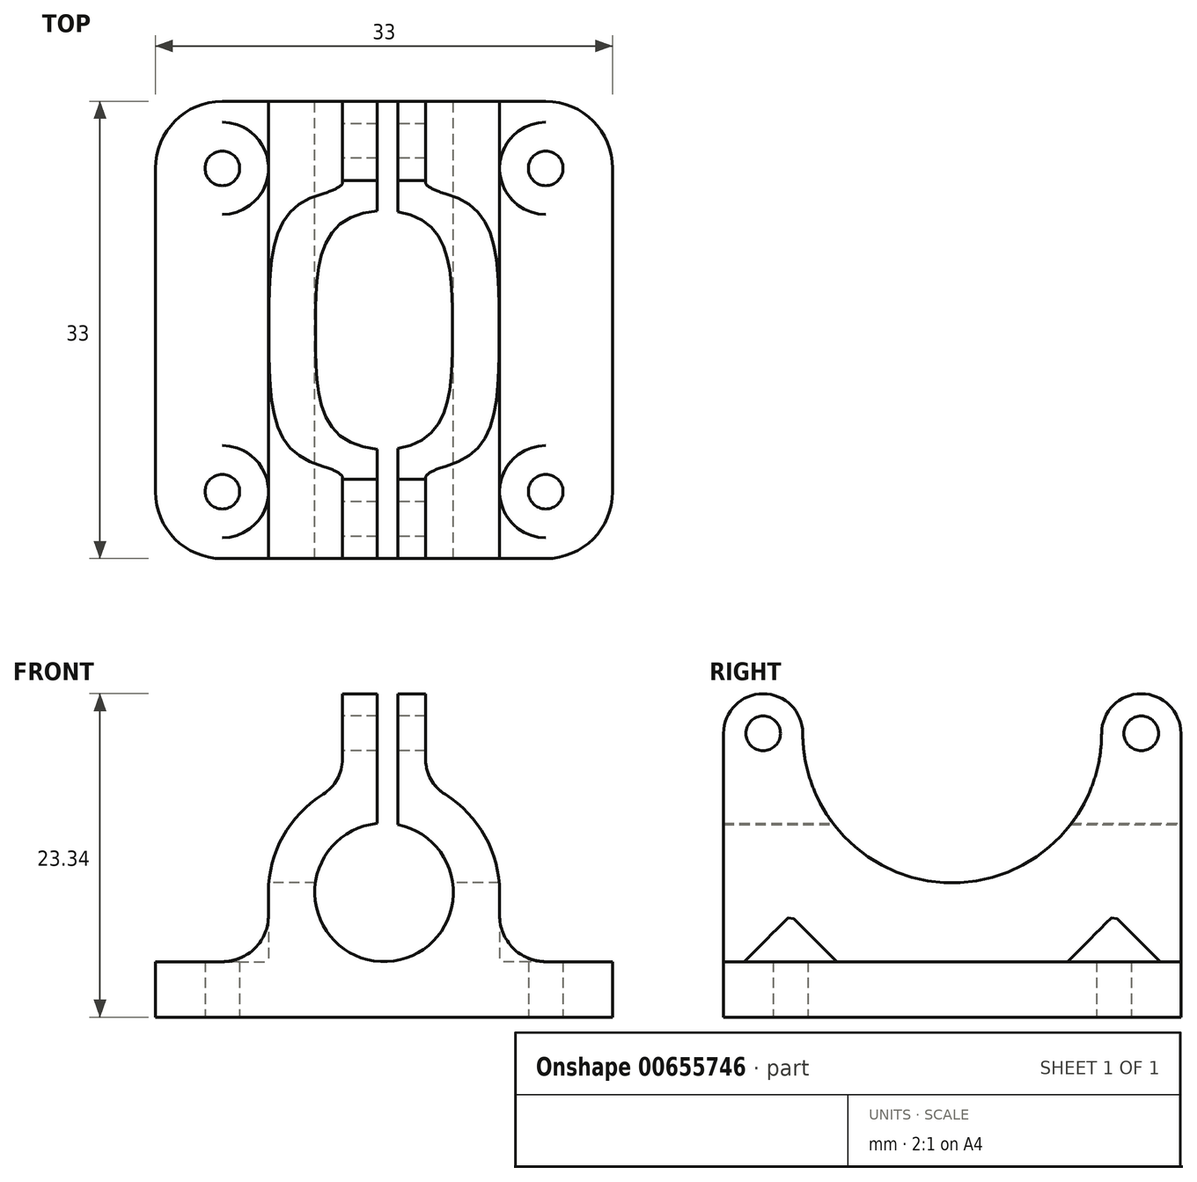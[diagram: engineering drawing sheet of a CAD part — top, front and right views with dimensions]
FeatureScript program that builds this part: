
annotation { "Feature Type Name" : "Feature", "Feature Type Description" : "" }
export const myFeature = defineFeature(function(context is Context, id is Id, definition is map)
    precondition{}
    {
        {
            var Q0;
            Q0=qCreatedBy(makeId("Top.planeOp"),FACE);
            var sketch = newSketch(context, id + "F0", { "sketchPlane" : qUnion([Q0])});
            skLineSegment(sketch, "E0", {"start": v(0, 0) * mm, "end": v(33, 33) * mm});
            skLineSegment(sketch, "E1", {"start": v(16.5, 16.5) * mm, "end": v(28.17, 28.17) * mm});
            skCircle(sketch, "E2", {"center": v(28.17, 28.17) * mm, "radius": 1.25 * mm});
            skCircle(sketch, "E3.1.0", {"center": v(4.83, 28.17) * mm, "radius": 1.25 * mm});
            skCircle(sketch, "E3.2.0", {"center": v(4.83, 4.83) * mm, "radius": 1.25 * mm});
            skCircle(sketch, "E3.3.0", {"center": v(28.17, 4.83) * mm, "radius": 1.25 * mm});
            skPoint(sketch, "E3.center", {"position": v(16.5, 16.5) * mm});
            skArc(sketch, "E4", {"start": v(28.17, 33) * mm, "mid": v(31.58, 31.58) * mm, "end": v(33, 28.17) * mm});
            skArc(sketch, "E5.1.0", {"start": v(0, 28.17) * mm, "mid": v(1.42, 31.58) * mm, "end": v(4.83, 33) * mm});
            skArc(sketch, "E5.2.0", {"start": v(4.83, 0) * mm, "mid": v(1.42, 1.42) * mm, "end": v(0, 4.83) * mm});
            skArc(sketch, "E5.3.0", {"start": v(33, 4.83) * mm, "mid": v(31.58, 1.42) * mm, "end": v(28.17, 0) * mm});
            skLineSegment(sketch, "E6", {"start": v(4.83, 33) * mm, "end": v(28.17, 33) * mm});
            skLineSegment(sketch, "E7", {"start": v(33, 28.17) * mm, "end": v(33, 4.83) * mm});
            skLineSegment(sketch, "E8", {"start": v(28.17, 0) * mm, "end": v(4.83, 0) * mm});
            skLineSegment(sketch, "E9", {"start": v(0, 4.83) * mm, "end": v(0, 28.17) * mm});
            skSolve(sketch);
        }
        {
            var Q0;
            Q0=makeQuery(id+"F0.imprint","IMPRINT",FACE,{"disambiguationData":[TD([[makeQuery(id+"F0.imprint","IMPRINT",EDGE,{"derivedFrom":sQuery(id+"F0.wireOp",EDGE,"E3.1.0")}),-1.0]])]});
            var Q1;
            Q1=makeQuery(id+"F0.imprint","IMPRINT",FACE,{"disambiguationData":[TD([[makeQuery(id+"F0.imprint","IMPRINT",EDGE,{"derivedFrom":sQuery(id+"F0.wireOp",EDGE,"E3.3.0")}),-1.0]])]});
            extrude(context, id + "F1", {"entities" : qUnion([Q0, Q1]), "depth" : 4 * mm, "offsetDistance" : 25 * mm});
        }
        {
            var Q0;
            Q0=qCreatedBy(makeId("Front.planeOp"),FACE);
            var sketch = newSketch(context, id + "F2", { "sketchPlane" : qUnion([Q0])});
            skLineSegment(sketch, "E10", {"start": v(0, 0) * mm, "end": v(0, 4) * mm});
            skCircle(sketch, "E11", {"center": v(16.5, 9) * mm, "radius": 5 * mm});
            skArc(sketch, "E12", {"start": v(4.82, 4) * mm, "mid": v(7.2, 4.98) * mm, "end": v(8.16, 7.36) * mm});
            skLineSegment(sketch, "E13", {"start": v(8.16, 7.36) * mm, "end": v(8.16, 9) * mm});
            skArc(sketch, "E14", {"start": v(24.84, 9) * mm, "mid": v(16.5, 17.34) * mm, "end": v(8.16, 9) * mm});
            skArc(sketch, "E15.MirrorCS", {"start": v(28.18, 4) * mm, "mid": v(25.8, 4.98) * mm, "end": v(24.84, 7.36) * mm});
            skLineSegment(sketch, "E16.MirrorCS", {"start": v(24.84, 7.36) * mm, "end": v(24.84, 9) * mm});
            skLineSegment(sketch, "E17", {"start": v(4.82, 4) * mm, "end": v(28.18, 4) * mm});
            skSolve(sketch);
        }
        {
            var Q0;
            Q0 = qSketchRegion(id + "F2", true);
            extrude(context, id + "F3", {"entities" : qUnion([Q0]), "operationType" : NewBodyOperationType.ADD, "oppositeDirection" : true, "depth" : 33 * mm, "offsetDistance" : 25 * mm});
        }
        {
            var Q0;
            Q0=makeQuery(id+"F3.boolean.opBoolean","MERGE",FACE,{"derivedFrom":[makeQuery(id+"F1.opExtrude","SWEPT_FACE",FACE,{"disambiguationData":[OSD([sQuery(id+"F0.wireOp",EDGE,"E6")])]}),makeQuery(id+"F3.opExtrude","CAP_FACE",FACE,{"disambiguationData":[OSD([sQuery(id+"F2.wireOp",EDGE,"E12"),sQuery(id+"F2.wireOp",EDGE,"E13"),sQuery(id+"F2.wireOp",EDGE,"E14"),sQuery(id+"F2.wireOp",EDGE,"E15.MirrorCS"),sQuery(id+"F2.wireOp",EDGE,"E16.MirrorCS"),sQuery(id+"F2.wireOp",EDGE,"E17")])],"isStart":false})]});
            var sketch = newSketch(context, id + "F4", { "sketchPlane" : qUnion([Q0])});
            skPoint(sketch, "E18.first.point", {"position": v(-24.84, 9) * mm});
            skPoint(sketch, "E18.second.point", {"position": v(-8.16, 9) * mm});
            skPoint(sketch, "E18.third.point", {"position": v(-15.36, 17.26) * mm});
            skCircle(sketch, "E19", {"center": v(-16.5, 9) * mm, "radius": 5 * mm});
            skSolve(sketch);
        }
        {
            var Q0;
            Q0 = qSketchRegion(id + "F4", true);
            extrude(context, id + "F5", {"entities" : qUnion([Q0]), "operationType" : NewBodyOperationType.REMOVE, "endBound" : BoundingType.THROUGH_ALL, "oppositeDirection" : true, "depth" : 25 * mm, "offsetDistance" : 25 * mm});
        }
        {
            var Q0;
            Q0=makeQuery(id+"F1.opExtrude","CAP_FACE",FACE,{"disambiguationData":[OSD([sQuery(id+"F0.wireOp",EDGE,"E2"),sQuery(id+"F0.wireOp",EDGE,"E3.1.0"),sQuery(id+"F0.wireOp",EDGE,"E3.2.0"),sQuery(id+"F0.wireOp",EDGE,"E3.3.0"),sQuery(id+"F0.wireOp",EDGE,"E4"),sQuery(id+"F0.wireOp",EDGE,"E5.1.0"),sQuery(id+"F0.wireOp",EDGE,"E5.2.0"),sQuery(id+"F0.wireOp",EDGE,"E5.3.0"),sQuery(id+"F0.wireOp",EDGE,"E6"),sQuery(id+"F0.wireOp",EDGE,"E7"),sQuery(id+"F0.wireOp",EDGE,"E8"),sQuery(id+"F0.wireOp",EDGE,"E9")])],"isStart":true});
            var sketch = newSketch(context, id + "F6", { "sketchPlane" : qUnion([Q0])});
            skCircle(sketch, "E20", {"center": v(28.17, -4.83) * mm, "radius": 1.25 * mm});
            skPoint(sketch, "E20.first.point", {"position": v(27.08, -4.22) * mm});
            skPoint(sketch, "E20.second.point", {"position": v(29.02, -5.75) * mm});
            skPoint(sketch, "E20.third.point", {"position": v(29.04, -3.94) * mm});
            skLineSegment(sketch, "E21", {"start": v(28.17, -4.83) * mm, "end": v(4.83, -28.17) * mm});
            skCircle(sketch, "E22.1.0", {"center": v(4.83, -4.83) * mm, "radius": 1.25 * mm});
            skCircle(sketch, "E22.2.0", {"center": v(4.83, -28.17) * mm, "radius": 1.25 * mm});
            skCircle(sketch, "E22.3.0", {"center": v(28.17, -28.17) * mm, "radius": 1.25 * mm});
            skPoint(sketch, "E22.center", {"position": v(16.5, -16.5) * mm});
            skSolve(sketch);
        }
        {
            var Q0;
            Q0=makeQuery(id+"F6.imprint","IMPRINT",FACE,{"disambiguationData":[TD([[makeQuery(id+"F6.imprint","IMPRINT",EDGE,{"derivedFrom":sQuery(id+"F6.wireOp",EDGE,"E22.1.0")}),-1.0]])]});
            var Q1;
            Q1=makeQuery(id+"F6.imprint","IMPRINT",FACE,{"disambiguationData":[TD([[makeQuery(id+"F6.imprint","IMPRINT",EDGE,{"derivedFrom":sQuery(id+"F6.wireOp",EDGE,"E20")}),-1.0]])]});
            var Q2;
            Q2=makeQuery(id+"F6.imprint","IMPRINT",FACE,{"disambiguationData":[TD([[makeQuery(id+"F6.imprint","IMPRINT",EDGE,{"derivedFrom":sQuery(id+"F6.wireOp",EDGE,"E22.3.0")}),-1.0]])]});
            var Q3;
            Q3=makeQuery(id+"F6.imprint","IMPRINT",FACE,{"disambiguationData":[TD([[makeQuery(id+"F6.imprint","IMPRINT",EDGE,{"derivedFrom":sQuery(id+"F6.wireOp",EDGE,"E22.2.0")}),-1.0]])]});
            extrude(context, id + "F7", {"entities" : qUnion([Q0, Q1, Q2, Q3]), "operationType" : NewBodyOperationType.REMOVE, "endBound" : BoundingType.THROUGH_ALL, "oppositeDirection" : true, "depth" : 25 * mm, "offsetDistance" : 25 * mm});
        }
        {
            var Q0;
            Q0=makeQuery(id+"F3.boolean.opBoolean","MERGE",FACE,{"derivedFrom":[makeQuery(id+"F1.opExtrude","SWEPT_FACE",FACE,{"disambiguationData":[OSD([sQuery(id+"F0.wireOp",EDGE,"E6")])]}),makeQuery(id+"F3.opExtrude","CAP_FACE",FACE,{"disambiguationData":[OSD([sQuery(id+"F2.wireOp",EDGE,"E12"),sQuery(id+"F2.wireOp",EDGE,"E13"),sQuery(id+"F2.wireOp",EDGE,"E14"),sQuery(id+"F2.wireOp",EDGE,"E15.MirrorCS"),sQuery(id+"F2.wireOp",EDGE,"E16.MirrorCS"),sQuery(id+"F2.wireOp",EDGE,"E17")])],"isStart":false})]});
            var sketch = newSketch(context, id + "F8", { "sketchPlane" : qUnion([Q0])});
            skLineSegment(sketch, "E23", {"start": v(-16.5, 23.34) * mm, "end": v(-14.5, 23.34) * mm});
            skLineSegment(sketch, "E24", {"start": v(-13.5, 22.34) * mm, "end": v(-13.5, 18.62) * mm});
            skPoint(sketch, "E25.visualSharp", {"position": v(-13.5, 16.78) * mm});
            skArc(sketch, "E25.filletArc", {"start": v(-13.5, 18.62) * mm, "mid": v(-13.12, 17.16) * mm, "end": v(-12.09, 16.07) * mm});
            skArc(sketch, "E26", {"start": v(-12.09, 16.07) * mm, "mid": v(-14.2, 17.02) * mm, "end": v(-16.5, 17.34) * mm});
            skPoint(sketch, "E27.visualSharp", {"position": v(-13.5, 23.34) * mm});
            skLineSegment(sketch, "E28.MirrorCS", {"start": v(-16.5, 23.34) * mm, "end": v(-18.5, 23.34) * mm});
            skLineSegment(sketch, "E29.MirrorCS", {"start": v(-19.5, 22.34) * mm, "end": v(-19.5, 18.62) * mm});
            skArc(sketch, "E30.MirrorCS", {"start": v(-19.5, 18.62) * mm, "mid": v(-19.88, 17.16) * mm, "end": v(-20.91, 16.07) * mm});
            skArc(sketch, "E31.MirrorCS", {"start": v(-20.91, 16.07) * mm, "mid": v(-18.8, 17.02) * mm, "end": v(-16.5, 17.34) * mm});
            skLineSegment(sketch, "E32", {"start": v(-13.5, 22.34) * mm, "end": v(-13.5, 23.34) * mm});
            skLineSegment(sketch, "E33", {"start": v(-13.5, 23.34) * mm, "end": v(-19.5, 23.34) * mm});
            skLineSegment(sketch, "E34", {"start": v(-19.5, 23.34) * mm, "end": v(-19.5, 22.34) * mm});
            skSolve(sketch);
        }
        {
            var Q0;
            Q0 = qSketchRegion(id + "F8", true);
            extrude(context, id + "F9", {"entities" : qUnion([Q0]), "operationType" : NewBodyOperationType.ADD, "oppositeDirection" : true, "depth" : 33 * mm, "offsetDistance" : 25 * mm});
        }
        {
            var Q0;
            Q0=qCreatedBy(makeId("Right.planeOp"),FACE);
            var sketch = newSketch(context, id + "F10", { "sketchPlane" : qUnion([Q0])});
            skLineSegment(sketch, "E35", {"start": v(33, 23.34) * mm, "end": v(0, 23.34) * mm});
            skLineSegment(sketch, "E36", {"start": v(0, 23.34) * mm, "end": v(0, 20.48) * mm});
            skArc(sketch, "E37", {"start": v(33, 20.48) * mm, "mid": v(30.14, 23.34) * mm, "end": v(27.28, 20.48) * mm});
            skArc(sketch, "E38", {"start": v(27.28, 20.48) * mm, "mid": v(24.12, 12.85) * mm, "end": v(16.5, 9.7) * mm});
            skArc(sketch, "E39.MirrorCS", {"start": v(5.72, 20.48) * mm, "mid": v(8.88, 12.85) * mm, "end": v(16.5, 9.7) * mm});
            skArc(sketch, "E40.MirrorCS", {"start": v(0, 20.48) * mm, "mid": v(2.86, 23.34) * mm, "end": v(5.72, 20.48) * mm});
            skCircle(sketch, "E41", {"center": v(2.86, 20.48) * mm, "radius": 1.25 * mm});
            skCircle(sketch, "E42.MirrorC", {"center": v(30.14, 20.48) * mm, "radius": 1.25 * mm});
            skLineSegment(sketch, "E43", {"start": v(33, 20.48) * mm, "end": v(33, 23.34) * mm});
            skSolve(sketch);
        }
        {
            var Q0;
            Q0 = qSketchRegion(id + "F10", true);
            extrude(context, id + "F11", {"entities" : qUnion([Q0]), "operationType" : NewBodyOperationType.REMOVE, "depth" : 25 * mm, "offsetDistance" : 25 * mm});
        }
        {
            var Q0;
            Q0=makeQuery(id+"F9.boolean.opBoolean","MERGE",FACE,{"derivedFrom":[makeQuery(id+"F3.boolean.opBoolean","MERGE",FACE,{"derivedFrom":[makeQuery(id+"F1.opExtrude","SWEPT_FACE",FACE,{"disambiguationData":[OSD([sQuery(id+"F0.wireOp",EDGE,"E8")])]}),makeQuery(id+"F3.opExtrude","CAP_FACE",FACE,{"disambiguationData":[OSD([sQuery(id+"F2.wireOp",EDGE,"E12"),sQuery(id+"F2.wireOp",EDGE,"E13"),sQuery(id+"F2.wireOp",EDGE,"E14"),sQuery(id+"F2.wireOp",EDGE,"E15.MirrorCS"),sQuery(id+"F2.wireOp",EDGE,"E16.MirrorCS"),sQuery(id+"F2.wireOp",EDGE,"E17")])],"isStart":true})]}),makeQuery(id+"F9.opExtrude","CAP_FACE",FACE,{"disambiguationData":[OSD([sQuery(id+"F8.wireOp",EDGE,"E23"),sQuery(id+"F8.wireOp",EDGE,"E24"),sQuery(id+"F8.wireOp",EDGE,"E25.filletArc"),sQuery(id+"F8.wireOp",EDGE,"E26"),sQuery(id+"F8.wireOp",EDGE,"E27.filletArc"),sQuery(id+"F8.wireOp",EDGE,"E28.MirrorCS"),sQuery(id+"F8.wireOp",EDGE,"0b07fa1e-377d-49d1-a351-c928c3afa0d80.MirrorCS"),sQuery(id+"F8.wireOp",EDGE,"E29.MirrorCS"),sQuery(id+"F8.wireOp",EDGE,"E30.MirrorCS"),sQuery(id+"F8.wireOp",EDGE,"E31.MirrorCS")])],"isStart":false})]});
            var sketch = newSketch(context, id + "F12", { "sketchPlane" : qUnion([Q0])});
            skLineSegment(sketch, "E44", {"start": v(16.5, 9) * mm, "end": v(17.5, 9) * mm});
            skLineSegment(sketch, "E45", {"start": v(16.5, 9) * mm, "end": v(16, 9) * mm});
            skLineSegment(sketch, "E46", {"start": v(16, 9) * mm, "end": v(16, 23.6) * mm});
            skLineSegment(sketch, "E47", {"start": v(16, 23.6) * mm, "end": v(17.5, 23.6) * mm});
            skLineSegment(sketch, "E48", {"start": v(17.5, 23.6) * mm, "end": v(17.5, 9) * mm});
            skSolve(sketch);
        }
        {
            var Q0;
            Q0 = qSketchRegion(id + "F12", true);
            extrude(context, id + "F13", {"entities" : qUnion([Q0]), "operationType" : NewBodyOperationType.REMOVE, "endBound" : BoundingType.THROUGH_ALL, "oppositeDirection" : true, "depth" : 25 * mm, "offsetDistance" : 25 * mm});
        }
        {
            var Q0;
            {var subQ0=sQuery(id+"F0.wireOp",EDGE,"E5.3.0");var subQ1=sQuery(id+"F0.wireOp",EDGE,"E4");var subQ2=sQuery(id+"F0.wireOp",EDGE,"E3.3.0");var subQ3=sQuery(id+"F0.wireOp",EDGE,"E2");var subQ4=sQuery(id+"F0.wireOp",EDGE,"E7");Q0=makeQuery(id+"F3.boolean.opBoolean","SPLIT",FACE,{"disambiguationData":[TD([makeQuery(id+"F1.opExtrude","SWEPT_FACE",FACE,{"disambiguationData":[OSD([subQ3])]})])],"derivedFrom":makeQuery(id+"F1.opExtrude","CAP_FACE",FACE,{"disambiguationData":[OSD([subQ3,sQuery(id+"F0.wireOp",EDGE,"E3.1.0"),sQuery(id+"F0.wireOp",EDGE,"E3.2.0"),subQ2,subQ1,sQuery(id+"F0.wireOp",EDGE,"E5.1.0"),sQuery(id+"F0.wireOp",EDGE,"E5.2.0"),subQ0,sQuery(id+"F0.wireOp",EDGE,"E6"),subQ4,sQuery(id+"F0.wireOp",EDGE,"E8"),sQuery(id+"F0.wireOp",EDGE,"E9")])],"isStart":false})});}
            var sketch = newSketch(context, id + "F14", { "sketchPlane" : qUnion([Q0])});
            skArc(sketch, "E49.0", {"start": v(4.82, 29.42) * mm, "mid": v(3.58, 28.17) * mm, "end": v(4.82, 26.92) * mm});
            skCircle(sketch, "E50", {"center": v(4.83, 28.17) * mm, "radius": 3.33 * mm});
            skLineSegment(sketch, "E51", {"start": v(4.83, 28.17) * mm, "end": v(28.17, 4.83) * mm});
            skCircle(sketch, "E52.1.0", {"center": v(4.83, 4.83) * mm, "radius": 3.33 * mm});
            skCircle(sketch, "E52.2.0", {"center": v(28.17, 4.83) * mm, "radius": 3.33 * mm});
            skCircle(sketch, "E52.3.0", {"center": v(28.17, 28.17) * mm, "radius": 3.33 * mm});
            skPoint(sketch, "E52.center", {"position": v(16.5, 16.5) * mm});
            skSolve(sketch);
        }
        {
            var Q0;
            Q0 = qSketchRegion(id + "F14", true);
            extrude(context, id + "F15", {"entities" : qUnion([Q0]), "operationType" : NewBodyOperationType.REMOVE, "endBound" : BoundingType.THROUGH_ALL, "depth" : 25 * mm, "offsetDistance" : 25 * mm});
        }
    });
